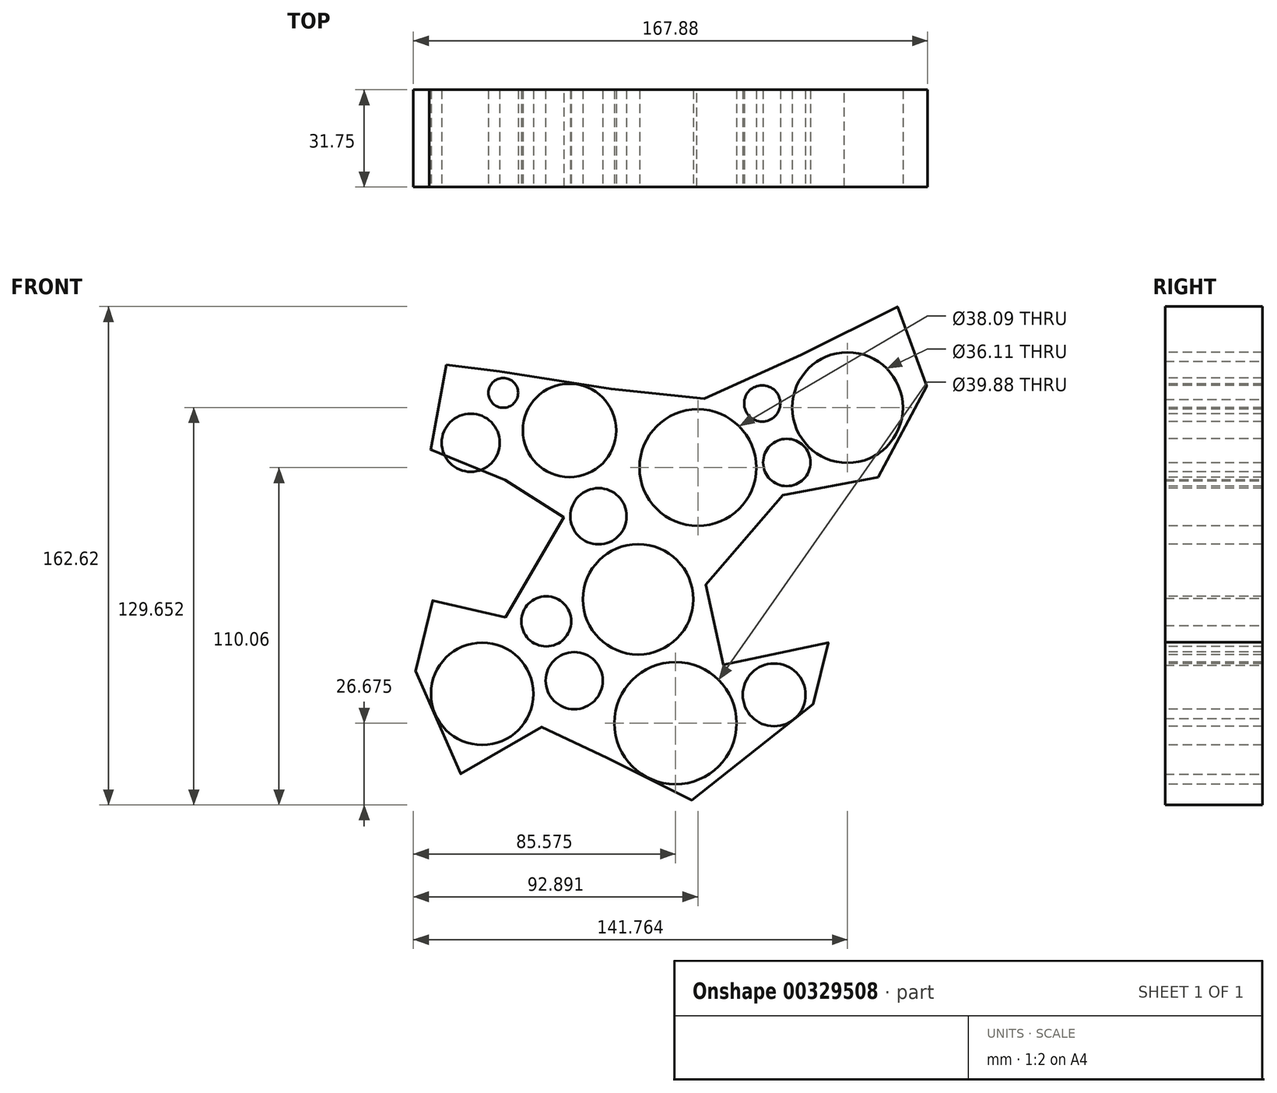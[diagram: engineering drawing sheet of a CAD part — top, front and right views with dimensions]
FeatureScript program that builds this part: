
annotation { "Feature Type Name" : "Feature", "Feature Type Description" : "" }
export const myFeature = defineFeature(function(context is Context, id is Id, definition is map)
    precondition{}
    {
        {
            var Q0;
            Q0=qCreatedBy(makeId("Front.planeOp"),FACE);
            var sketch = newSketch(context, id + "F0", { "sketchPlane" : qUnion([Q0])});
            skFitSpline(sketch, "E0", {"points": [v(-124.09, 62.62) * mm, v(-125.74, 27.95) * mm, v(-87.14, 21.45) * mm, v(-110.85, -22.35) * mm, v(-132.36, -14.22) * mm, v(-120.78, -70.44) * mm, v(-84.93, -52.92) * mm, v(-52.4, -81.03) * mm, v(5.51, -29.02) * mm, v(-37.5, -34.26) * mm, v(-22.06, 15.97) * mm, v(23.16, 30.12) * mm, v(27.02, 80.32) * mm, v(-24.27, 56.14) * mm, v(-67.28, 54.2) * mm, v(-119.12, 62.95) * mm, v(-124.09, 62.62) * mm]});
            skSolve(sketch);
        }
        {
            var Q0;
            Q0=makeQuery(id+"F0.imprint","IMPRINT",FACE,{"disambiguationData":[TD([[makeQuery(id+"F0.imprint","IMPRINT",EDGE,{"derivedFrom":sQuery(id+"F0.wireOp",EDGE,"E0")}),1.0]])]});
            extrude(context, id + "F1", {"entities" : qUnion([Q0]), "depth" : 31.75 * mm});
        }
        {
            var Q0;
            Q0=makeQuery(id+"F1.opExtrude","CAP_FACE",FACE,{"disambiguationData":[OSD([sQuery(id+"F0.wireOp",EDGE,"E0")])],"isStart":false});
            var sketch = newSketch(context, id + "F2", { "sketchPlane" : qUnion([Q0])});
            skCircle(sketch, "E1", {"center": v(-74.38, 13.15) * mm, "radius": 9.17 * mm});
            skCircle(sketch, "E2", {"center": v(-116.1, 37.15) * mm, "radius": 9.49 * mm});
            skCircle(sketch, "E3", {"center": v(6.93, 48.61) * mm, "radius": 18.05 * mm});
            skCircle(sketch, "E4", {"center": v(-41.94, 29.02) * mm, "radius": 19.05 * mm});
            skCircle(sketch, "E5", {"center": v(-12.91, 30.7) * mm, "radius": 7.72 * mm});
            skCircle(sketch, "E6", {"center": v(-20.94, 49.96) * mm, "radius": 5.9 * mm});
            skCircle(sketch, "E7", {"center": v(-83.85, 41.16) * mm, "radius": 15.25 * mm});
            skCircle(sketch, "E8", {"center": v(-105.47, 53.42) * mm, "radius": 4.85 * mm});
            skCircle(sketch, "E9", {"center": v(-49.26, -54.36) * mm, "radius": 19.94 * mm});
            skCircle(sketch, "E10", {"center": v(-61.45, -13.97) * mm, "radius": 18.02 * mm});
            skCircle(sketch, "E11", {"center": v(-112.36, -44.8) * mm, "radius": 16.72 * mm});
            skCircle(sketch, "E12", {"center": v(-82.3, -40.5) * mm, "radius": 9.32 * mm});
            skCircle(sketch, "E13", {"center": v(-91.44, -21.14) * mm, "radius": 8.16 * mm});
            skCircle(sketch, "E14", {"center": v(-17.04, -45.14) * mm, "radius": 10.24 * mm});
            skSolve(sketch);
        }
        {
            var Q0;
            Q0=makeQuery(id+"F2.imprint","IMPRINT",FACE,{"disambiguationData":[TD([[makeQuery(id+"F2.imprint","IMPRINT",EDGE,{"derivedFrom":sQuery(id+"F2.wireOp",EDGE,"E11")}),1.0]])]});
            var Q1;
            Q1=makeQuery(id+"F2.imprint","IMPRINT",FACE,{"disambiguationData":[TD([[makeQuery(id+"F2.imprint","IMPRINT",EDGE,{"derivedFrom":sQuery(id+"F2.wireOp",EDGE,"E13")}),1.0]])]});
            var Q2;
            Q2=makeQuery(id+"F2.imprint","IMPRINT",FACE,{"disambiguationData":[TD([[makeQuery(id+"F2.imprint","IMPRINT",EDGE,{"derivedFrom":sQuery(id+"F2.wireOp",EDGE,"E12")}),1.0]])]});
            var Q3;
            Q3=makeQuery(id+"F2.imprint","IMPRINT",FACE,{"disambiguationData":[TD([[makeQuery(id+"F2.imprint","IMPRINT",EDGE,{"derivedFrom":sQuery(id+"F2.wireOp",EDGE,"E9")}),1.0]])]});
            var Q4;
            Q4=makeQuery(id+"F2.imprint","IMPRINT",FACE,{"disambiguationData":[TD([[makeQuery(id+"F2.imprint","IMPRINT",EDGE,{"derivedFrom":sQuery(id+"F2.wireOp",EDGE,"E10")}),1.0]])]});
            var Q5;
            Q5=makeQuery(id+"F2.imprint","IMPRINT",FACE,{"disambiguationData":[TD([[makeQuery(id+"F2.imprint","IMPRINT",EDGE,{"derivedFrom":sQuery(id+"F2.wireOp",EDGE,"E1")}),1.0]])]});
            var Q6;
            Q6=makeQuery(id+"F2.imprint","IMPRINT",FACE,{"disambiguationData":[TD([[makeQuery(id+"F2.imprint","IMPRINT",EDGE,{"derivedFrom":sQuery(id+"F2.wireOp",EDGE,"E7")}),1.0]])]});
            var Q7;
            Q7=makeQuery(id+"F2.imprint","IMPRINT",FACE,{"disambiguationData":[TD([[makeQuery(id+"F2.imprint","IMPRINT",EDGE,{"derivedFrom":sQuery(id+"F2.wireOp",EDGE,"E2")}),1.0]])]});
            var Q8;
            Q8=makeQuery(id+"F2.imprint","IMPRINT",FACE,{"disambiguationData":[TD([[makeQuery(id+"F2.imprint","IMPRINT",EDGE,{"derivedFrom":sQuery(id+"F2.wireOp",EDGE,"E8")}),1.0]])]});
            var Q9;
            Q9=makeQuery(id+"F2.imprint","IMPRINT",FACE,{"disambiguationData":[TD([[makeQuery(id+"F2.imprint","IMPRINT",EDGE,{"derivedFrom":sQuery(id+"F2.wireOp",EDGE,"E4")}),1.0]])]});
            var Q10;
            Q10=makeQuery(id+"F2.imprint","IMPRINT",FACE,{"disambiguationData":[TD([[makeQuery(id+"F2.imprint","IMPRINT",EDGE,{"derivedFrom":sQuery(id+"F2.wireOp",EDGE,"E6")}),1.0]])]});
            var Q11;
            Q11=makeQuery(id+"F2.imprint","IMPRINT",FACE,{"disambiguationData":[TD([[makeQuery(id+"F2.imprint","IMPRINT",EDGE,{"derivedFrom":sQuery(id+"F2.wireOp",EDGE,"E5")}),1.0]])]});
            var Q12;
            Q12=makeQuery(id+"F2.imprint","IMPRINT",FACE,{"disambiguationData":[TD([[makeQuery(id+"F2.imprint","IMPRINT",EDGE,{"derivedFrom":sQuery(id+"F2.wireOp",EDGE,"E3")}),1.0]])]});
            var Q13;
            Q13=makeQuery(id+"F2.imprint","IMPRINT",FACE,{"disambiguationData":[TD([[makeQuery(id+"F2.imprint","IMPRINT",EDGE,{"derivedFrom":sQuery(id+"F2.wireOp",EDGE,"E14")}),1.0]])]});
            extrude(context, id + "F3", {"entities" : qUnion([Q0, Q1, Q2, Q3, Q4, Q5, Q6, Q7, Q8, Q9, Q10, Q11, Q12, Q13]), "operationType" : NewBodyOperationType.REMOVE, "oppositeDirection" : true, "depth" : 35.3 * mm});
        }
    });
